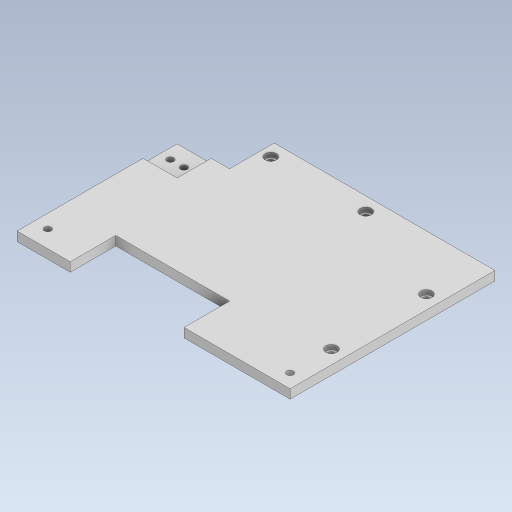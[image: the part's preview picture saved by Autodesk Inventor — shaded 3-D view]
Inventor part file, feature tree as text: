
AUTODESK INVENTOR PART (.ipt)
format: ipt  version: 2023.5 (Build 275446000, 446)  size: 367,616 bytes
history: native  units: in
note: dims shown in document units (in); Inventor stores cm internally (conversion verified against a paired STEP export)
features: extrude x2, sketch x1
ambient origin geometry x8: Origin, YZ Plane, XZ Plane, XY Plane, X Axis, Y Axis, Z Axis, Center Point
bodies: Body1 (feature_tree)
feature tree (3):
  sketch  "Sketch1"  dims[d0=4.7244in d1=3.5433in d21=0.1181in d22=0.2559in d23=0.1181in d24=0.2559in d25=0.1181in d27=0.1181in d32=0.1969in d38=0.1181in d39=0.1969in d40=0.2362in d41=0.1969in d42=0.1181in d43=0.2362in d44=0.2362in d45=0.1181in d46=0.2362in d59=0.7736in d60=0.1181in d61=0.1969in d63=0.2953in d64=0.1575in d65=0.0in d66=0.0787in d67=0.0in d68=0.1181in d69=0.1181in d70=0.8219in d71=0.8219in d72=0.1969in d73=0.1969in d74=0.0in d75=0.0in d76=0.2953in d77=0.2953in d78=0.2953in d79=0.2953in d81=0.315in d33=0.0197in d34=0.0344in d35=0.0197in d36=0.0344in]
  extrude  "Extrusion3"  Depth=3.5433in
  extrude  "Extrusion4"  Depth=0.315in
